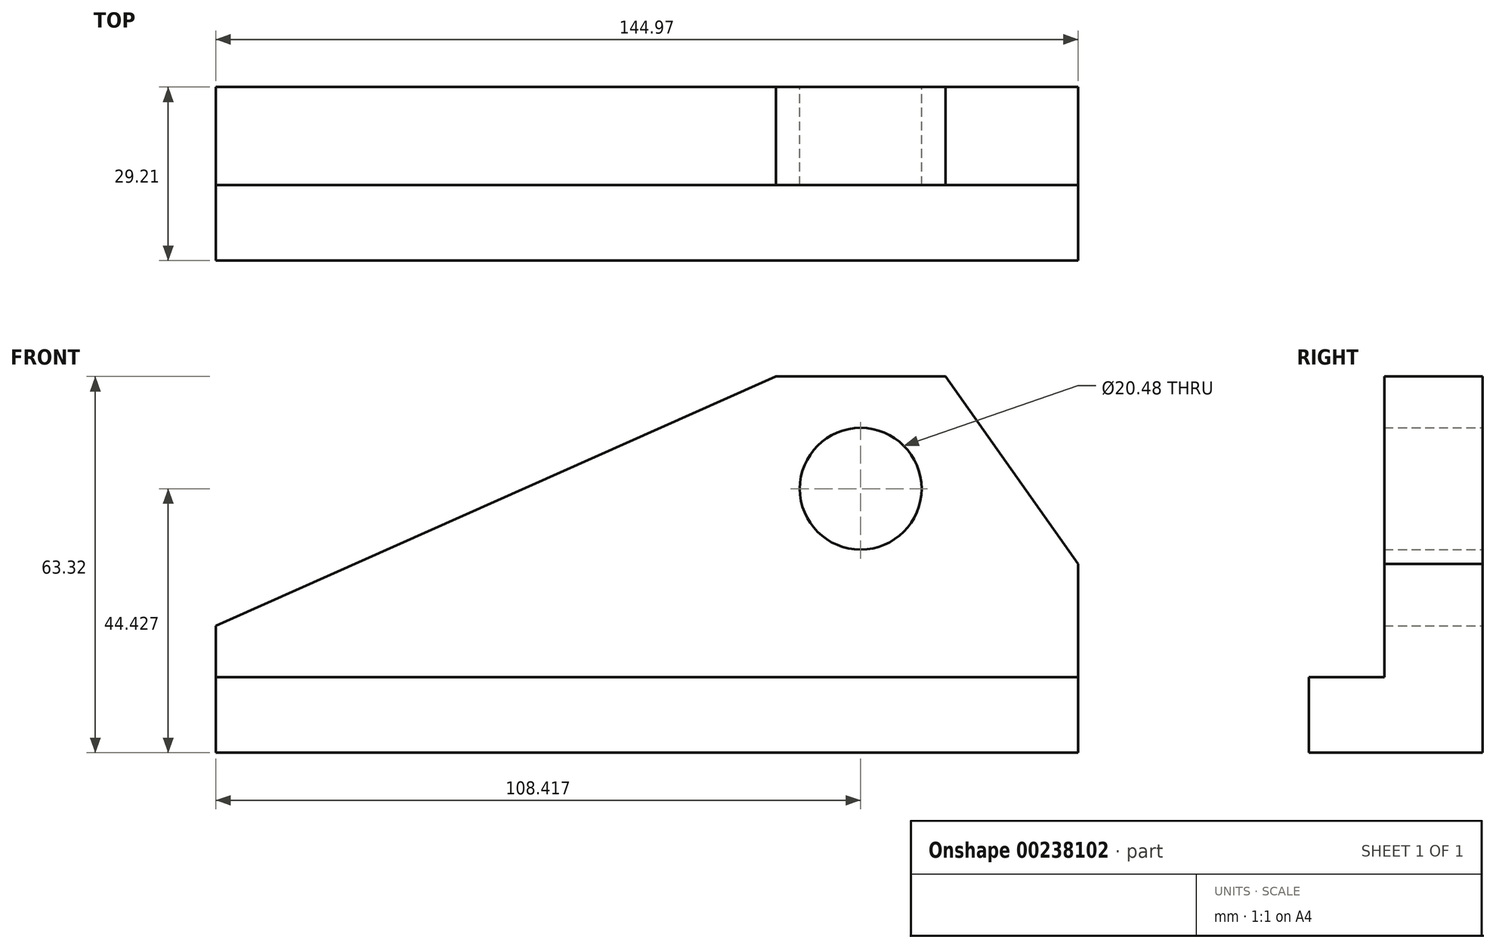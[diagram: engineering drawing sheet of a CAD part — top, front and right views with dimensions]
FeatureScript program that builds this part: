
annotation { "Feature Type Name" : "Feature", "Feature Type Description" : "" }
export const myFeature = defineFeature(function(context is Context, id is Id, definition is map)
    precondition{}
    {
        {
            var Q0;
            Q0=qCreatedBy(makeId("Front.planeOp"),FACE);
            var sketch = newSketch(context, id + "F0", { "sketchPlane" : qUnion([Q0])});
            skLineSegment(sketch, "E0", {"start": v(21.53, 41.97) * mm, "end": v(50.06, 41.97) * mm});
            skLineSegment(sketch, "E1", {"start": v(50.06, 41.97) * mm, "end": v(72.33, 10.4) * mm});
            skLineSegment(sketch, "E2", {"start": v(72.33, 10.4) * mm, "end": v(72.33, -8.65) * mm});
            skLineSegment(sketch, "E3", {"start": v(72.33, -8.65) * mm, "end": v(-72.64, -8.65) * mm});
            skLineSegment(sketch, "E4", {"start": v(-72.64, -8.65) * mm, "end": v(-72.64, 0) * mm});
            skLineSegment(sketch, "E5", {"start": v(-72.64, 0) * mm, "end": v(21.53, 41.97) * mm});
            skLineSegment(sketch, "E6", {"start": v(-72.64, -8.65) * mm, "end": v(-72.64, -21.35) * mm});
            skLineSegment(sketch, "E7", {"start": v(72.33, -2.63) * mm, "end": v(72.33, -8.65) * mm});
            skLineSegment(sketch, "E8", {"start": v(-72.64, -21.35) * mm, "end": v(72.33, -21.35) * mm});
            skLineSegment(sketch, "E9", {"start": v(72.33, -8.65) * mm, "end": v(72.33, -21.35) * mm});
            skCircle(sketch, "E10", {"center": v(35.78, 23.08) * mm, "radius": 10.24 * mm});
            skSolve(sketch);
        }
        {
            var Q0;
            Q0=makeQuery(id+"F0.imprint","IMPRINT",FACE,{"disambiguationData":[TD([[makeQuery(id+"F0.imprint","IMPRINT",EDGE,{"derivedFrom":sQuery(id+"F0.wireOp",EDGE,"E3")}),1.0]])]});
            extrude(context, id + "F1", {"entities" : qUnion([Q0]), "depth" : 29.2 * mm, "offsetDistance" : 25.4 * mm});
        }
        {
            var Q0;
            Q0 = qSketchRegion(id + "F0", true);
            extrude(context, id + "F2", {"entities" : qUnion([Q0]), "operationType" : NewBodyOperationType.ADD, "depth" : 16.5 * mm, "offsetDistance" : 25.4 * mm});
        }
    });
